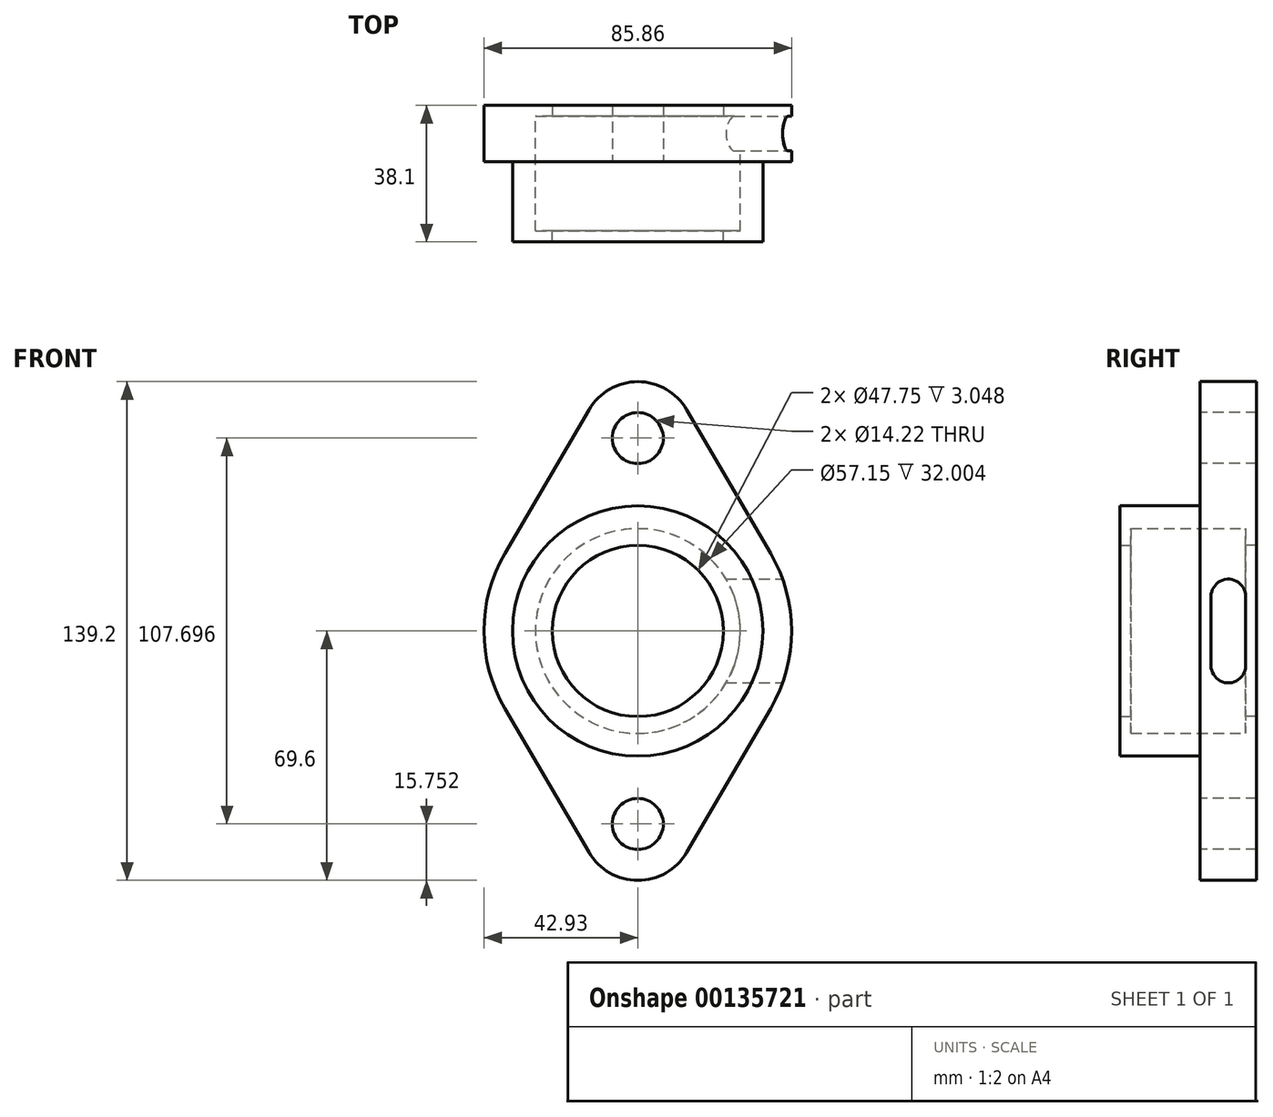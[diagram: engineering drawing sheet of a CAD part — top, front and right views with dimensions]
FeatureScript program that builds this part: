
annotation { "Feature Type Name" : "Feature", "Feature Type Description" : "" }
export const myFeature = defineFeature(function(context is Context, id is Id, definition is map)
    precondition{}
    {
        {
            var Q0;
            Q0=qCreatedBy(makeId("Front.planeOp"),FACE);
            var sketch = newSketch(context, id + "F0", { "sketchPlane" : qUnion([Q0])});
            skLineSegment(sketch, "E0", {"start": v(0, 50.05) * mm, "end": v(0, -53.85) * mm, "construction": true});
            skLineSegment(sketch, "E1", {"start": v(-48.85, 0) * mm, "end": v(63.83, 0) * mm, "construction": true});
            skLineSegment(sketch, "E2", {"start": v(-13.6, 61.8) * mm, "end": v(-37.06, 21.67) * mm});
            skLineSegment(sketch, "E3", {"start": v(-37.06, -21.67) * mm, "end": v(-13.6, -61.8) * mm});
            skLineSegment(sketch, "E4", {"start": v(13.6, 61.8) * mm, "end": v(37.06, 21.67) * mm});
            skLineSegment(sketch, "E5", {"start": v(37.06, -21.67) * mm, "end": v(13.6, -61.8) * mm});
            skArc(sketch, "E6", {"start": v(13.6, 61.8) * mm, "mid": v(0, 69.6) * mm, "end": v(-13.6, 61.8) * mm});
            skArc(sketch, "E7", {"start": v(-13.6, -61.8) * mm, "mid": v(0, -69.6) * mm, "end": v(13.6, -61.8) * mm});
            skCircle(sketch, "E8", {"center": v(0, 0) * mm, "radius": 23.88 * mm});
            skCircle(sketch, "E9", {"center": v(0, 53.85) * mm, "radius": 7.11 * mm});
            skCircle(sketch, "E10", {"center": v(0, -53.85) * mm, "radius": 7.11 * mm});
            skCircle(sketch, "E11", {"center": v(0, 0) * mm, "radius": 34.93 * mm});
            skCircle(sketch, "E12", {"center": v(0, 0) * mm, "radius": 28.58 * mm});
            skArc(sketch, "E13", {"start": v(-37.06, 21.67) * mm, "mid": v(-42.93, 0) * mm, "end": v(-37.06, -21.67) * mm});
            skArc(sketch, "E14", {"start": v(37.06, -21.67) * mm, "mid": v(42.93, 0) * mm, "end": v(37.06, 21.67) * mm});
            skSolve(sketch);
        }
        {
            var Q0;
            Q0=makeQuery(id+"F0.imprint","IMPRINT",FACE,{"disambiguationData":[TD([[makeQuery(id+"F0.imprint","IMPRINT",EDGE,{"derivedFrom":sQuery(id+"F0.wireOp",EDGE,"E2")}),1.0]])]});
            var Q1;
            Q1=makeQuery(id+"F0.imprint","IMPRINT",FACE,{"disambiguationData":[TD([[makeQuery(id+"F0.imprint","IMPRINT",EDGE,{"derivedFrom":sQuery(id+"F0.wireOp",EDGE,"E11")}),1.0]])]});
            var Q2;
            Q2=makeQuery(id+"F0.imprint","IMPRINT",FACE,{"disambiguationData":[TD([[makeQuery(id+"F0.imprint","IMPRINT",EDGE,{"derivedFrom":sQuery(id+"F0.wireOp",EDGE,"E8")}),-1.0]])]});
            extrude(context, id + "F1", {"entities" : qUnion([Q0, Q1, Q2]), "oppositeDirection" : true, "depth" : 15.75 * mm});
        }
        {
            var Q0;
            Q0=makeQuery(id+"F0.imprint","IMPRINT",FACE,{"disambiguationData":[TD([[makeQuery(id+"F0.imprint","IMPRINT",EDGE,{"derivedFrom":sQuery(id+"F0.wireOp",EDGE,"E11")}),1.0]])]});
            extrude(context, id + "F2", {"entities" : qUnion([Q0]), "operationType" : NewBodyOperationType.ADD, "depth" : 22.35 * mm});
        }
        {
            var Q0;
            Q0=makeQuery(id+"F0.imprint","IMPRINT",FACE,{"disambiguationData":[TD([[makeQuery(id+"F0.imprint","IMPRINT",EDGE,{"derivedFrom":sQuery(id+"F0.wireOp",EDGE,"E8")}),-1.0]])]});
            extrude(context, id + "F3", {"entities" : qUnion([Q0]), "operationType" : NewBodyOperationType.REMOVE, "oppositeDirection" : true, "depth" : 12.7 * mm});
        }
        {
            var Q0;
            Q0=makeQuery(id+"F0.imprint","IMPRINT",FACE,{"disambiguationData":[TD([[makeQuery(id+"F0.imprint","IMPRINT",EDGE,{"derivedFrom":sQuery(id+"F0.wireOp",EDGE,"E8")}),-1.0]])]});
            extrude(context, id + "F4", {"entities" : qUnion([Q0]), "operationType" : NewBodyOperationType.ADD, "depth" : 22.35 * mm});
        }
        {
            var Q0;
            Q0=makeQuery(id+"F0.imprint","IMPRINT",FACE,{"disambiguationData":[TD([[makeQuery(id+"F0.imprint","IMPRINT",EDGE,{"derivedFrom":sQuery(id+"F0.wireOp",EDGE,"E8")}),-1.0]])]});
            extrude(context, id + "F5", {"entities" : qUnion([Q0]), "operationType" : NewBodyOperationType.REMOVE, "depth" : 19.3 * mm});
        }
        {
            var Q0;
            Q0=qCreatedBy(makeId("Right.planeOp"),FACE);
            cPlane(context, id + "F6", {"entities" : qUnion([Q0]), "cplaneType" : CPlaneType.OFFSET, "offset" : 28.57 * mm, "width" : 152.4 * mm, "height" : 152.4 * mm});
        }
        {
            var Q0;
            Q0=qCreatedBy(id+"F6.planeOp",FACE);
            var sketch = newSketch(context, id + "F7", { "sketchPlane" : qUnion([Q0])});
            skLineSegment(sketch, "E15.0", {"start": v(15.75, 61.8) * mm, "end": v(0, 61.8) * mm});
            skLineSegment(sketch, "E16", {"start": v(7.87, 76.36) * mm, "end": v(7.87, -94.3) * mm, "construction": true});
            skPoint(sketch, "E16.startSnap0", {"position": v(7.87, 61.8) * mm});
            skLineSegment(sketch, "E17", {"start": v(-28.86, 0) * mm, "end": v(63.4, 0) * mm, "construction": true});
            skLineSegment(sketch, "E18", {"start": v(3.05, 9.65) * mm, "end": v(3.05, -9.65) * mm});
            skLineSegment(sketch, "E19", {"start": v(12.7, -9.65) * mm, "end": v(12.7, 9.65) * mm});
            skArc(sketch, "E20", {"start": v(3.05, 9.65) * mm, "mid": v(7.87, 14.48) * mm, "end": v(12.7, 9.65) * mm});
            skArc(sketch, "E21", {"start": v(3.05, -9.65) * mm, "mid": v(7.87, -14.48) * mm, "end": v(12.7, -9.65) * mm});
            skSolve(sketch);
        }
        {
            var Q0;
            Q0 = qSketchRegion(id + "F7", true);
            extrude(context, id + "F8", {"entities" : qUnion([Q0]), "operationType" : NewBodyOperationType.REMOVE, "endBound" : BoundingType.SYMMETRIC, "oppositeDirection" : true, "depth" : 38.1 * mm});
        }
    });
